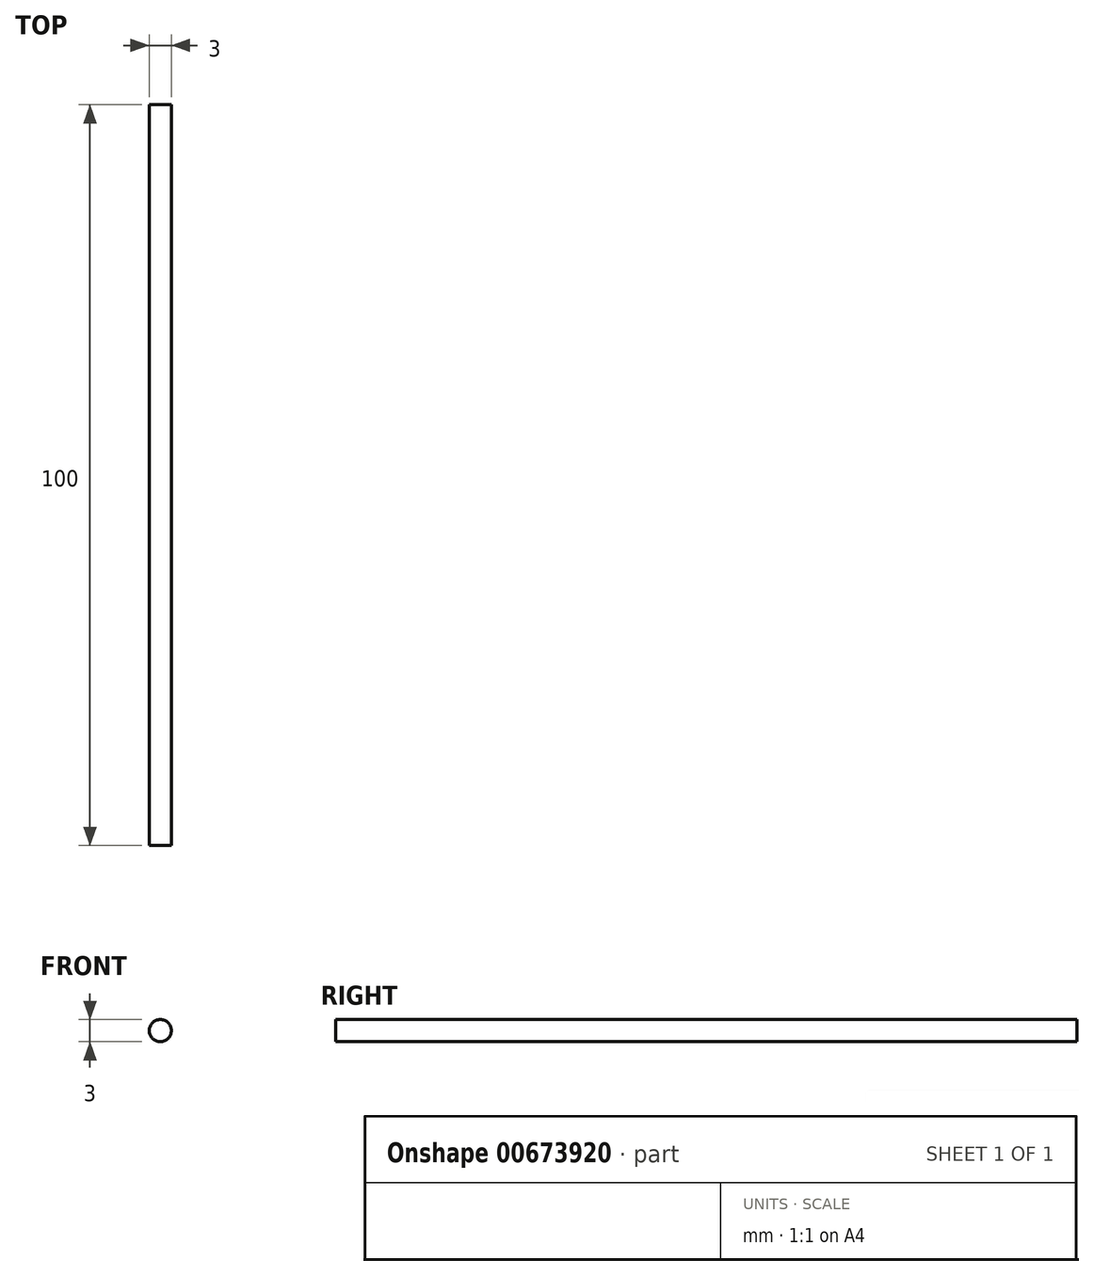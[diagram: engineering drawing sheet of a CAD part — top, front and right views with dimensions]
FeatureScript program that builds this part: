
annotation { "Feature Type Name" : "Feature", "Feature Type Description" : "" }
export const myFeature = defineFeature(function(context is Context, id is Id, definition is map)
    precondition{}
    {
        {
            var Q0;
            Q0=qCreatedBy(makeId("Front.planeOp"),FACE);
            var sketch = newSketch(context, id + "F0", { "sketchPlane" : qUnion([Q0])});
            skCircle(sketch, "E0", {"center": v(0, 0) * mm, "radius": 1.5 * mm});
            skSolve(sketch);
        }
        {
            var Q0;
            Q0 = qSketchRegion(id + "F0", true);
            extrude(context, id + "F1", {"entities" : qUnion([Q0]), "depth" : 100 * mm, "offsetDistance" : 25 * mm});
        }
    });
